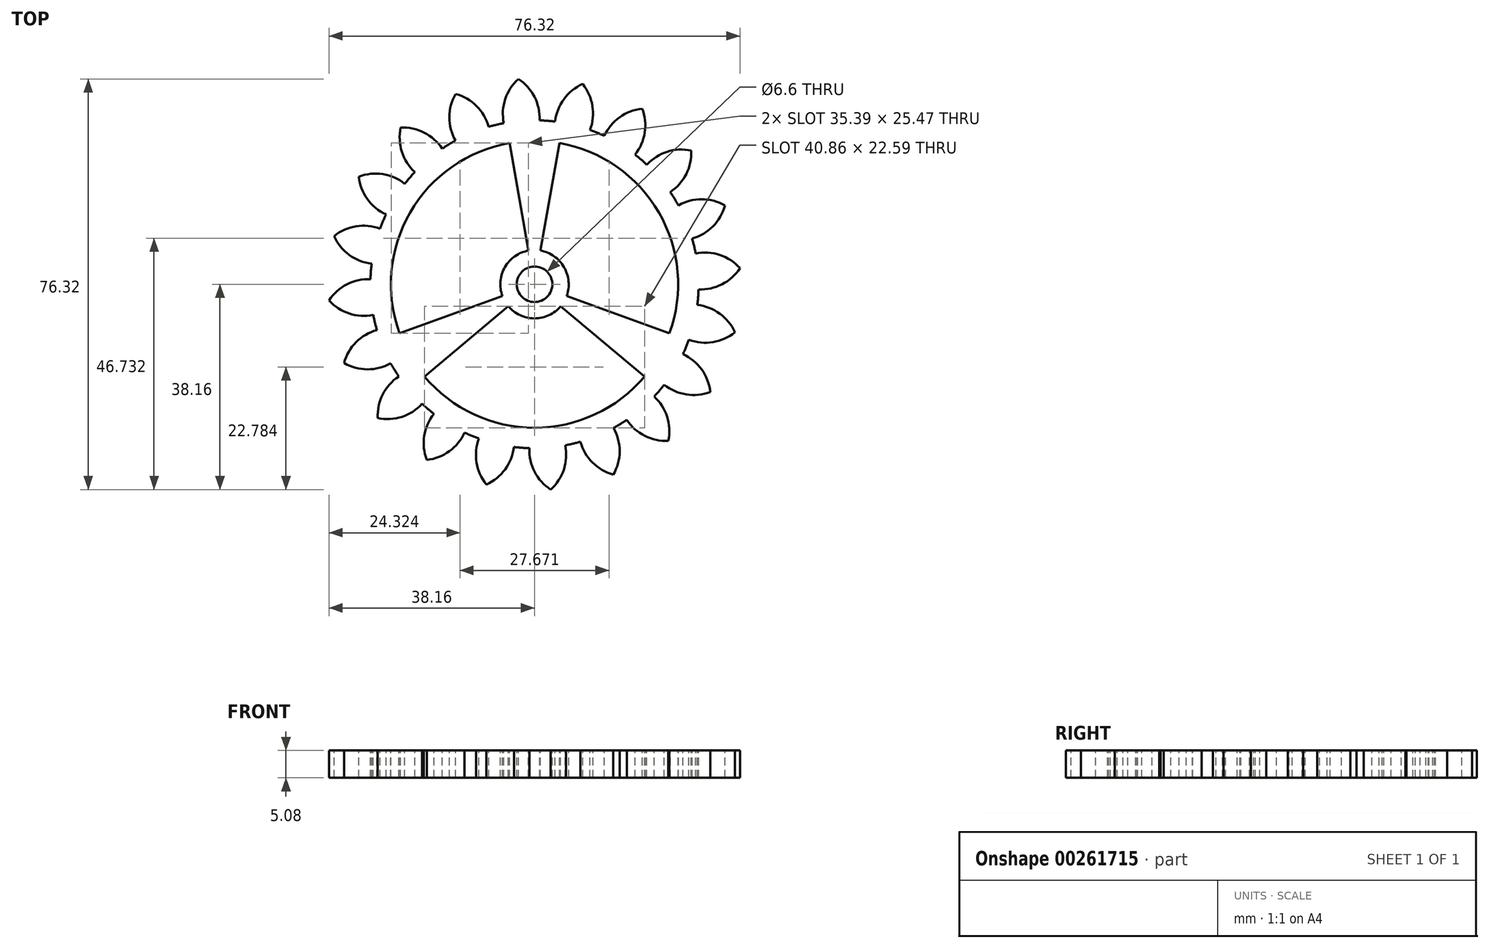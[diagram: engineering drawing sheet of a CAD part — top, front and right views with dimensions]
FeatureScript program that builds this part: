
annotation { "Feature Type Name" : "Feature", "Feature Type Description" : "" }
export const myFeature = defineFeature(function(context is Context, id is Id, definition is map)
    precondition{}
    {
        {
            var Q0;
            Q0=qCreatedBy(makeId("Top.planeOp"),FACE);
            var sketch = newSketch(context, id + "F0", { "sketchPlane" : qUnion([Q0])});
            skCircle(sketch, "E0", {"center": v(0, 0) * mm, "radius": 30.48 * mm});
            skSolve(sketch);
        }
        {
            var Q0;
            Q0=qSketchRegion(id+"F0",true);
            extrude(context, id + "F1", {"entities" : qUnion([Q0]), "depth" : 5.08 * mm});
        }
        {
            var Q0;
            Q0=makeQuery(id+"F1.opExtrude","CAP_FACE",FACE,{"disambiguationData":[OSD([sQuery(id+"F0.wireOp",EDGE,"E0")])],"isStart":false});
            var sketch = newSketch(context, id + "F2", { "sketchPlane" : qUnion([Q0])});
            skCircle(sketch, "E1", {"center": v(0, 0) * mm, "radius": 38.31 * mm, "construction": true});
            skCircle(sketch, "E2", {"center": v(0, 0) * mm, "radius": 34.83 * mm, "construction": true});
            skCircle(sketch, "E3", {"center": v(0, 0) * mm, "radius": 30.48 * mm, "construction": true});
            skLineSegment(sketch, "E4", {"start": v(0, 0) * mm, "end": v(0, 56.9) * mm, "construction": true});
            skLineSegment(sketch, "E5", {"start": v(0, 0) * mm, "end": v(-4.62, 58.65) * mm, "construction": true});
            skLineSegment(sketch, "E6", {"start": v(0, 34.83) * mm, "end": v(-65.71, 34.83) * mm, "construction": true});
            skLineSegment(sketch, "E7", {"start": v(0, 34.83) * mm, "end": v(-58.85, 8.63) * mm, "construction": true});
            skCircle(sketch, "E8", {"center": v(0, 34.83) * mm, "radius": 8.7 * mm, "construction": true});
            skCircle(sketch, "E9", {"center": v(0, 0) * mm, "radius": 31.82 * mm, "construction": true});
            skCircle(sketch, "E10", {"center": v(-7.75, 30.86) * mm, "radius": 8.7 * mm, "construction": true});
            skArc(sketch, "E11", {"start": v(0.95, 30.46) * mm, "mid": v(0, 34.84) * mm, "end": v(-3, 38.16) * mm});
            skArc(sketch, "E12.MirrorCS", {"start": v(-5.7, 29.94) * mm, "mid": v(-5.45, 34.4) * mm, "end": v(-3, 38.16) * mm});
            skLineSegment(sketch, "E13", {"start": v(-5.7, 29.94) * mm, "end": v(0.95, 30.46) * mm});
            skPoint(sketch, "E14.orphan", {"position": v(-2.96, 38.2) * mm});
            skPoint(sketch, "E15.orphan", {"position": v(-3.05, 38.2) * mm});
            skSolve(sketch);
        }
        {
            var Q0;
            Q0=qSketchRegion(id+"F2",true);
            var Q1;
            Q1=makeQuery(id+"F1.opExtrude","CAP_FACE",FACE,{"disambiguationData":[OSD([sQuery(id+"F0.wireOp",EDGE,"E0")])],"isStart":true});
            extrude(context, id + "F3", {"entities" : qUnion([Q0]), "endBound" : BoundingType.UP_TO_SURFACE, "oppositeDirection" : true, "endBoundEntityFace" : qUnion([Q1]), "depth" : 25.4 * mm});
        }
        {
            var Q0;
            Q0=makeQuery(id+"F3.opExtrude","SWEPT_BODY",BODY,{"disambiguationData":[OSD([sQuery(id+"F2.wireOp",EDGE,"E11"),sQuery(id+"F2.wireOp",EDGE,"E12.MirrorCS"),sQuery(id+"F2.wireOp",EDGE,"E13")])]});
            var Q1;
            Q1=makeQuery(id+"F1.opExtrude","CAP_EDGE",EDGE,{"disambiguationData":[OSD([sQuery(id+"F0.wireOp",EDGE,"E0")])],"isStart":false});
            circularPattern(context, id + "F4", {"operationType" : NewBodyOperationType.ADD, "entities" : qUnion([Q0]), "axis" : qUnion([Q1]), "angle" : 360 * degree, "instanceCount" : 20, "equalSpace" : true});
        }
        {
            var Q0;
            {var subQ0=makeQuery(id+"F3.opExtrude","CAP_FACE",FACE,{"disambiguationData":[OSD([sQuery(id+"F2.wireOp",EDGE,"E11"),sQuery(id+"F2.wireOp",EDGE,"E12.MirrorCS"),sQuery(id+"F2.wireOp",EDGE,"E13")])],"isStart":true});Q0=makeQuery(id+"F4.boolean.opBoolean","MERGE",FACE,{"derivedFrom":[makeQuery(id+"F1.opExtrude","CAP_FACE",FACE,{"disambiguationData":[OSD([sQuery(id+"F0.wireOp",EDGE,"E0")])],"isStart":false}),subQ0,makeQuery(id+"F4.opPattern","COPY",FACE,{"derivedFrom":subQ0,"instanceName":"1"}),makeQuery(id+"F4.opPattern","COPY",FACE,{"derivedFrom":subQ0,"instanceName":"2"}),makeQuery(id+"F4.opPattern","COPY",FACE,{"derivedFrom":subQ0,"instanceName":"3"}),makeQuery(id+"F4.opPattern","COPY",FACE,{"derivedFrom":subQ0,"instanceName":"4"}),makeQuery(id+"F4.opPattern","COPY",FACE,{"derivedFrom":subQ0,"instanceName":"5"}),makeQuery(id+"F4.opPattern","COPY",FACE,{"derivedFrom":subQ0,"instanceName":"6"}),makeQuery(id+"F4.opPattern","COPY",FACE,{"derivedFrom":subQ0,"instanceName":"7"}),makeQuery(id+"F4.opPattern","COPY",FACE,{"derivedFrom":subQ0,"instanceName":"8"}),makeQuery(id+"F4.opPattern","COPY",FACE,{"derivedFrom":subQ0,"instanceName":"9"}),makeQuery(id+"F4.opPattern","COPY",FACE,{"derivedFrom":subQ0,"instanceName":"10"}),makeQuery(id+"F4.opPattern","COPY",FACE,{"derivedFrom":subQ0,"instanceName":"11"}),makeQuery(id+"F4.opPattern","COPY",FACE,{"derivedFrom":subQ0,"instanceName":"12"}),makeQuery(id+"F4.opPattern","COPY",FACE,{"derivedFrom":subQ0,"instanceName":"13"}),makeQuery(id+"F4.opPattern","COPY",FACE,{"derivedFrom":subQ0,"instanceName":"14"}),makeQuery(id+"F4.opPattern","COPY",FACE,{"derivedFrom":subQ0,"instanceName":"15"}),makeQuery(id+"F4.opPattern","COPY",FACE,{"derivedFrom":subQ0,"instanceName":"16"}),makeQuery(id+"F4.opPattern","COPY",FACE,{"derivedFrom":subQ0,"instanceName":"17"}),makeQuery(id+"F4.opPattern","COPY",FACE,{"derivedFrom":subQ0,"instanceName":"18"}),makeQuery(id+"F4.opPattern","COPY",FACE,{"derivedFrom":subQ0,"instanceName":"19"})]});}
            var sketch = newSketch(context, id + "F5", { "sketchPlane" : qUnion([Q0])});
            skCircle(sketch, "E16", {"center": v(0, 0) * mm, "radius": 26.67 * mm});
            skSolve(sketch);
        }
        {
            var Q0;
            Q0=qSketchRegion(id+"F5",true);
            extrude(context, id + "F6", {"entities" : qUnion([Q0]), "operationType" : NewBodyOperationType.REMOVE, "endBound" : BoundingType.THROUGH_ALL, "oppositeDirection" : true, "depth" : 25.4 * mm});
        }
        {
            var Q0;
            Q0 = qSketchRegion(id + "F5", true);
            extrude(context, id + "F7", {"entities" : qUnion([Q0]), "operationType" : NewBodyOperationType.REMOVE, "endBound" : BoundingType.THROUGH_ALL, "oppositeDirection" : true, "depth" : 25.4 * mm});
        }
        {
            var Q0;
            {var subQ0=makeQuery(id+"F3.opExtrude","CAP_FACE",FACE,{"disambiguationData":[OSD([sQuery(id+"F2.wireOp",EDGE,"E11"),sQuery(id+"F2.wireOp",EDGE,"E12.MirrorCS"),sQuery(id+"F2.wireOp",EDGE,"E13")])],"isStart":true});Q0=makeQuery(id+"F4.boolean.opBoolean","MERGE",FACE,{"derivedFrom":[makeQuery(id+"F1.opExtrude","CAP_FACE",FACE,{"disambiguationData":[OSD([sQuery(id+"F0.wireOp",EDGE,"E0")])],"isStart":false}),subQ0,makeQuery(id+"F4.opPattern","COPY",FACE,{"derivedFrom":subQ0,"instanceName":"1"}),makeQuery(id+"F4.opPattern","COPY",FACE,{"derivedFrom":subQ0,"instanceName":"2"}),makeQuery(id+"F4.opPattern","COPY",FACE,{"derivedFrom":subQ0,"instanceName":"3"}),makeQuery(id+"F4.opPattern","COPY",FACE,{"derivedFrom":subQ0,"instanceName":"4"}),makeQuery(id+"F4.opPattern","COPY",FACE,{"derivedFrom":subQ0,"instanceName":"5"}),makeQuery(id+"F4.opPattern","COPY",FACE,{"derivedFrom":subQ0,"instanceName":"6"}),makeQuery(id+"F4.opPattern","COPY",FACE,{"derivedFrom":subQ0,"instanceName":"7"}),makeQuery(id+"F4.opPattern","COPY",FACE,{"derivedFrom":subQ0,"instanceName":"8"}),makeQuery(id+"F4.opPattern","COPY",FACE,{"derivedFrom":subQ0,"instanceName":"9"}),makeQuery(id+"F4.opPattern","COPY",FACE,{"derivedFrom":subQ0,"instanceName":"10"}),makeQuery(id+"F4.opPattern","COPY",FACE,{"derivedFrom":subQ0,"instanceName":"11"}),makeQuery(id+"F4.opPattern","COPY",FACE,{"derivedFrom":subQ0,"instanceName":"12"}),makeQuery(id+"F4.opPattern","COPY",FACE,{"derivedFrom":subQ0,"instanceName":"13"}),makeQuery(id+"F4.opPattern","COPY",FACE,{"derivedFrom":subQ0,"instanceName":"14"}),makeQuery(id+"F4.opPattern","COPY",FACE,{"derivedFrom":subQ0,"instanceName":"15"}),makeQuery(id+"F4.opPattern","COPY",FACE,{"derivedFrom":subQ0,"instanceName":"16"}),makeQuery(id+"F4.opPattern","COPY",FACE,{"derivedFrom":subQ0,"instanceName":"17"}),makeQuery(id+"F4.opPattern","COPY",FACE,{"derivedFrom":subQ0,"instanceName":"18"}),makeQuery(id+"F4.opPattern","COPY",FACE,{"derivedFrom":subQ0,"instanceName":"19"})]});}
            var sketch = newSketch(context, id + "F8", { "sketchPlane" : qUnion([Q0])});
            skArc(sketch, "E17", {"start": v(-1.1, 6.25) * mm, "mid": v(0, -6.35) * mm, "end": v(1.1, 6.25) * mm});
            skLineSegment(sketch, "E18", {"start": v(-1.1, 6.25) * mm, "end": v(-4.63, 26.26) * mm});
            skArc(sketch, "E19", {"start": v(4.63, 26.26) * mm, "mid": v(0, 26.67) * mm, "end": v(-4.63, 26.26) * mm});
            skLineSegment(sketch, "E20", {"start": v(4.63, 26.26) * mm, "end": v(1.1, 6.25) * mm});
            skSolve(sketch);
        }
        {
            var Q0;
            Q0 = qSketchRegion(id + "F8", true);
            var Q1;
            {var subQ0=makeQuery(id+"F3.opExtrude","CAP_FACE",FACE,{"disambiguationData":[OSD([sQuery(id+"F2.wireOp",EDGE,"E11"),sQuery(id+"F2.wireOp",EDGE,"E12.MirrorCS"),sQuery(id+"F2.wireOp",EDGE,"E13")])],"isStart":false});Q1=makeQuery(id+"F4.boolean.opBoolean","MERGE",FACE,{"derivedFrom":[makeQuery(id+"F1.opExtrude","CAP_FACE",FACE,{"disambiguationData":[OSD([sQuery(id+"F0.wireOp",EDGE,"E0")])],"isStart":true}),subQ0,makeQuery(id+"F4.opPattern","COPY",FACE,{"derivedFrom":subQ0,"instanceName":"1"}),makeQuery(id+"F4.opPattern","COPY",FACE,{"derivedFrom":subQ0,"instanceName":"2"}),makeQuery(id+"F4.opPattern","COPY",FACE,{"derivedFrom":subQ0,"instanceName":"3"}),makeQuery(id+"F4.opPattern","COPY",FACE,{"derivedFrom":subQ0,"instanceName":"4"}),makeQuery(id+"F4.opPattern","COPY",FACE,{"derivedFrom":subQ0,"instanceName":"5"}),makeQuery(id+"F4.opPattern","COPY",FACE,{"derivedFrom":subQ0,"instanceName":"6"}),makeQuery(id+"F4.opPattern","COPY",FACE,{"derivedFrom":subQ0,"instanceName":"7"}),makeQuery(id+"F4.opPattern","COPY",FACE,{"derivedFrom":subQ0,"instanceName":"8"}),makeQuery(id+"F4.opPattern","COPY",FACE,{"derivedFrom":subQ0,"instanceName":"9"}),makeQuery(id+"F4.opPattern","COPY",FACE,{"derivedFrom":subQ0,"instanceName":"10"}),makeQuery(id+"F4.opPattern","COPY",FACE,{"derivedFrom":subQ0,"instanceName":"11"}),makeQuery(id+"F4.opPattern","COPY",FACE,{"derivedFrom":subQ0,"instanceName":"12"}),makeQuery(id+"F4.opPattern","COPY",FACE,{"derivedFrom":subQ0,"instanceName":"13"}),makeQuery(id+"F4.opPattern","COPY",FACE,{"derivedFrom":subQ0,"instanceName":"14"}),makeQuery(id+"F4.opPattern","COPY",FACE,{"derivedFrom":subQ0,"instanceName":"15"}),makeQuery(id+"F4.opPattern","COPY",FACE,{"derivedFrom":subQ0,"instanceName":"16"}),makeQuery(id+"F4.opPattern","COPY",FACE,{"derivedFrom":subQ0,"instanceName":"17"}),makeQuery(id+"F4.opPattern","COPY",FACE,{"derivedFrom":subQ0,"instanceName":"18"}),makeQuery(id+"F4.opPattern","COPY",FACE,{"derivedFrom":subQ0,"instanceName":"19"})]});}
            extrude(context, id + "F9", {"entities" : qUnion([Q0]), "endBound" : BoundingType.UP_TO_SURFACE, "oppositeDirection" : true, "endBoundEntityFace" : qUnion([Q1]), "depth" : 25.4 * mm});
        }
        {
            var Q0;
            Q0=makeQuery(id+"F9.opExtrude","SWEPT_BODY",BODY,{"disambiguationData":[OSD([sQuery(id+"F8.wireOp",EDGE,"E17"),sQuery(id+"F8.wireOp",EDGE,"E18"),sQuery(id+"F8.wireOp",EDGE,"E19"),sQuery(id+"F8.wireOp",EDGE,"E20")])]});
            var Q1;
            Q1=makeQuery(id+"F9.opExtrude","SWEPT_FACE",FACE,{"disambiguationData":[OSD([sQuery(id+"F8.wireOp",EDGE,"E17")])]});
            circularPattern(context, id + "F10", {"operationType" : NewBodyOperationType.ADD, "entities" : qUnion([Q0]), "axis" : qUnion([Q1]), "angle" : 360 * degree, "instanceCount" : 3, "equalSpace" : true});
        }
        {
            var Q0;
            {var subQ0=makeQuery(id+"F9.opExtrude","CAP_FACE",FACE,{"disambiguationData":[OSD([sQuery(id+"F8.wireOp",EDGE,"E17"),sQuery(id+"F8.wireOp",EDGE,"E18"),sQuery(id+"F8.wireOp",EDGE,"E19"),sQuery(id+"F8.wireOp",EDGE,"E20")])],"isStart":true});var subQ1=makeQuery(id+"F3.opExtrude","CAP_FACE",FACE,{"disambiguationData":[OSD([sQuery(id+"F2.wireOp",EDGE,"E11"),sQuery(id+"F2.wireOp",EDGE,"E12.MirrorCS"),sQuery(id+"F2.wireOp",EDGE,"E13")])],"isStart":true});Q0=makeQuery(id+"F10.boolean.opBoolean","MERGE",FACE,{"derivedFrom":[makeQuery(id+"F4.boolean.opBoolean","MERGE",FACE,{"derivedFrom":[makeQuery(id+"F1.opExtrude","CAP_FACE",FACE,{"disambiguationData":[OSD([sQuery(id+"F0.wireOp",EDGE,"E0")])],"isStart":false}),subQ1,makeQuery(id+"F4.opPattern","COPY",FACE,{"derivedFrom":subQ1,"instanceName":"1"}),makeQuery(id+"F4.opPattern","COPY",FACE,{"derivedFrom":subQ1,"instanceName":"2"}),makeQuery(id+"F4.opPattern","COPY",FACE,{"derivedFrom":subQ1,"instanceName":"3"}),makeQuery(id+"F4.opPattern","COPY",FACE,{"derivedFrom":subQ1,"instanceName":"4"}),makeQuery(id+"F4.opPattern","COPY",FACE,{"derivedFrom":subQ1,"instanceName":"5"}),makeQuery(id+"F4.opPattern","COPY",FACE,{"derivedFrom":subQ1,"instanceName":"6"}),makeQuery(id+"F4.opPattern","COPY",FACE,{"derivedFrom":subQ1,"instanceName":"7"}),makeQuery(id+"F4.opPattern","COPY",FACE,{"derivedFrom":subQ1,"instanceName":"8"}),makeQuery(id+"F4.opPattern","COPY",FACE,{"derivedFrom":subQ1,"instanceName":"9"}),makeQuery(id+"F4.opPattern","COPY",FACE,{"derivedFrom":subQ1,"instanceName":"10"}),makeQuery(id+"F4.opPattern","COPY",FACE,{"derivedFrom":subQ1,"instanceName":"11"}),makeQuery(id+"F4.opPattern","COPY",FACE,{"derivedFrom":subQ1,"instanceName":"12"}),makeQuery(id+"F4.opPattern","COPY",FACE,{"derivedFrom":subQ1,"instanceName":"13"}),makeQuery(id+"F4.opPattern","COPY",FACE,{"derivedFrom":subQ1,"instanceName":"14"}),makeQuery(id+"F4.opPattern","COPY",FACE,{"derivedFrom":subQ1,"instanceName":"15"}),makeQuery(id+"F4.opPattern","COPY",FACE,{"derivedFrom":subQ1,"instanceName":"16"}),makeQuery(id+"F4.opPattern","COPY",FACE,{"derivedFrom":subQ1,"instanceName":"17"}),makeQuery(id+"F4.opPattern","COPY",FACE,{"derivedFrom":subQ1,"instanceName":"18"}),makeQuery(id+"F4.opPattern","COPY",FACE,{"derivedFrom":subQ1,"instanceName":"19"})]}),subQ0,makeQuery(id+"F10.opPattern","COPY",FACE,{"derivedFrom":subQ0,"instanceName":"1"}),makeQuery(id+"F10.opPattern","COPY",FACE,{"derivedFrom":subQ0,"instanceName":"2"})]});}
            var sketch = newSketch(context, id + "F11", { "sketchPlane" : qUnion([Q0])});
            skCircle(sketch, "E21", {"center": v(0, 0) * mm, "radius": 3.3 * mm});
            skSolve(sketch);
        }
        {
            var Q0;
            Q0 = qSketchRegion(id + "F11", true);
            extrude(context, id + "F12", {"entities" : qUnion([Q0]), "operationType" : NewBodyOperationType.REMOVE, "endBound" : BoundingType.THROUGH_ALL, "oppositeDirection" : true, "depth" : 25.4 * mm});
        }
    });
